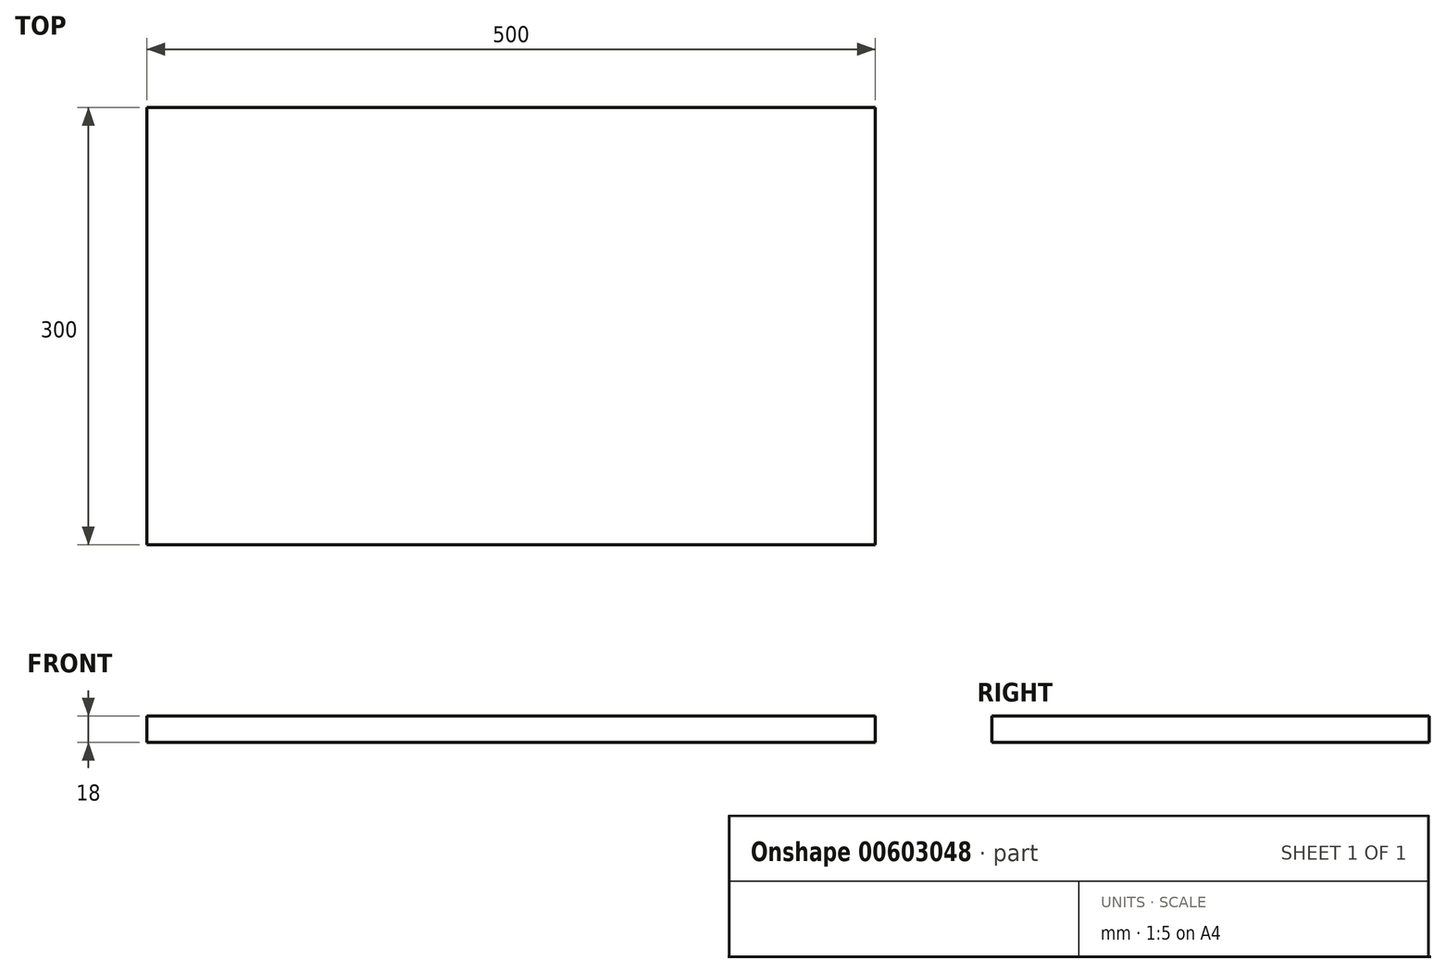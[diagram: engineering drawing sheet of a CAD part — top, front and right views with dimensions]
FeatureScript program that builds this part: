
annotation { "Feature Type Name" : "Feature", "Feature Type Description" : "" }
export const myFeature = defineFeature(function(context is Context, id is Id, definition is map)
    precondition{}
    {
        {
            var Q0;
            Q0=qCreatedBy(makeId("Top.planeOp"),FACE);
            var sketch = newSketch(context, id + "F0", { "sketchPlane" : qUnion([Q0])});
            skLineSegment(sketch, "E0.bottom", {"start": v(0, 0) * mm, "end": v(500, 0) * mm});
            skLineSegment(sketch, "E0.top", {"start": v(0, -300) * mm, "end": v(500, -300) * mm});
            skLineSegment(sketch, "E0.left", {"start": v(0, 0) * mm, "end": v(0, -300) * mm});
            skLineSegment(sketch, "E0.right", {"start": v(500, 0) * mm, "end": v(500, -300) * mm});
            skSolve(sketch);
        }
        {
            var Q0;
            Q0=makeQuery(id+"F0.imprint","IMPRINT",FACE,{"disambiguationData":[TD([[makeQuery(id+"F0.imprint","IMPRINT",EDGE,{"derivedFrom":sQuery(id+"F0.wireOp",EDGE,"E0.bottom")}),-1.0]])]});
            var Q1;
            Q1=makeQuery(id+"F0.imprint","IMPRINT",FACE,{"disambiguationData":[TD([[makeQuery(id+"F0.imprint","IMPRINT",EDGE,{"derivedFrom":sQuery(id+"F0.wireOp",EDGE,"E0.bottom")}),-1.0]])]});
            var Q2;
            Q2=sQuery(id+"F0.wireOp",EDGE,"E0.bottom");
            extrude(context, id + "F1", {"entities" : qUnion([Q0, Q1]), "surfaceEntities" : qUnion([Q2]), "depth" : 18 * mm, "offsetDistance" : 25 * mm});
        }
    });
